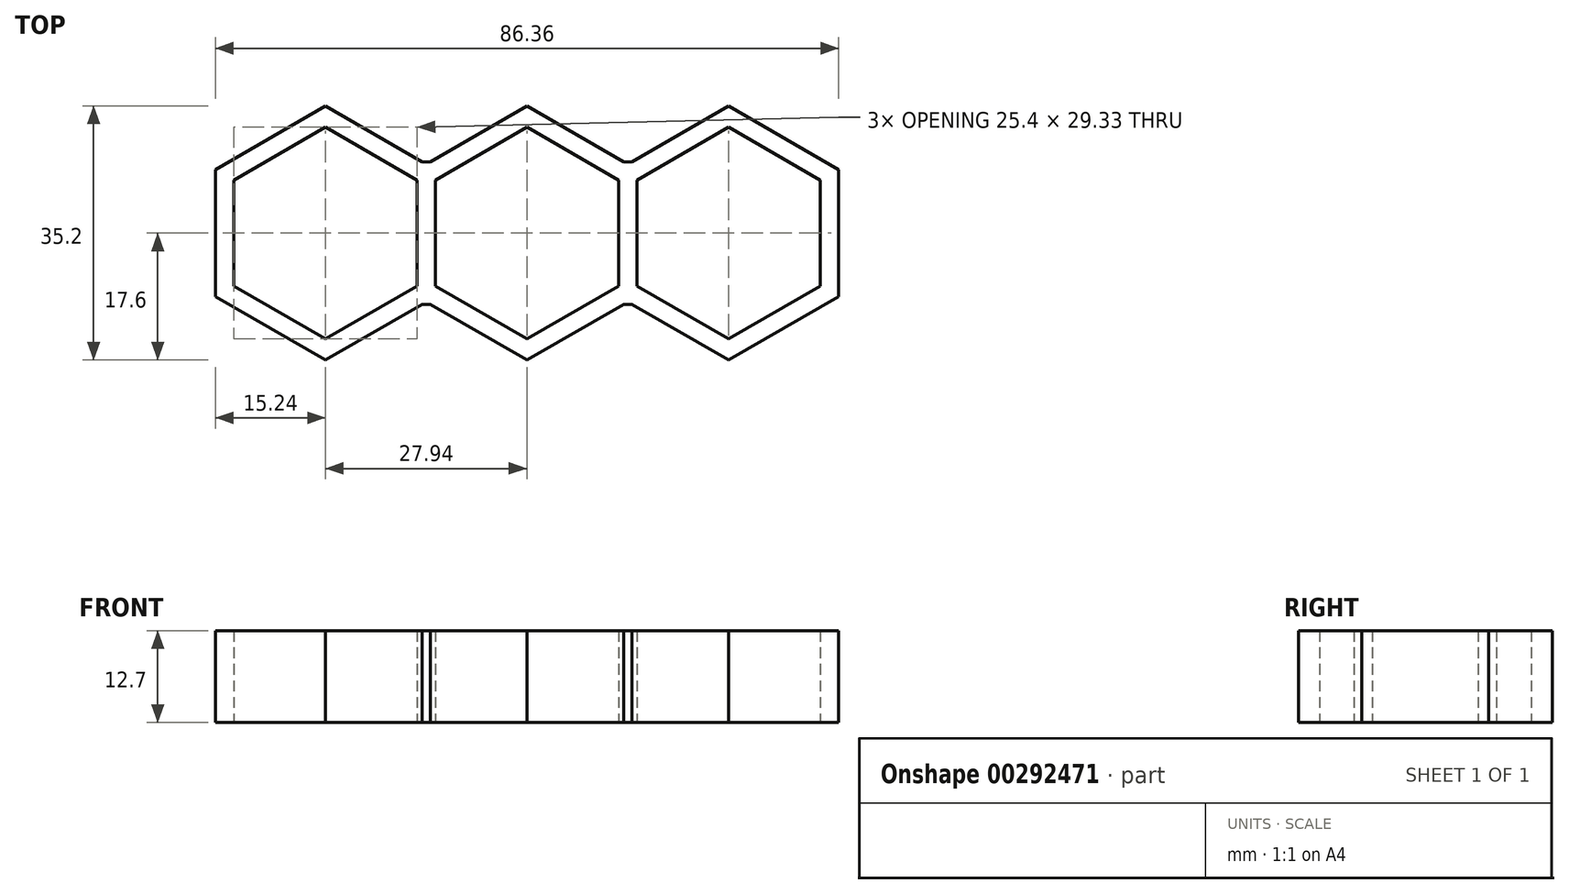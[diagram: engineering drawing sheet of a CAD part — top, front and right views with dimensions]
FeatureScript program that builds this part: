
annotation { "Feature Type Name" : "Feature", "Feature Type Description" : "" }
export const myFeature = defineFeature(function(context is Context, id is Id, definition is map)
    precondition{}
    {
        {
            var Q0;
            Q0=qCreatedBy(makeId("Top.planeOp"),FACE);
            var sketch = newSketch(context, id + "F0", { "sketchPlane" : qUnion([Q0])});
            skCircle(sketch, "E0.cCircle", {"center": v(0, 0) * mm, "radius": 12.7 * mm, "construction": true});
            skLineSegment(sketch, "E0.0", {"start": v(-12.7, -7.33) * mm, "end": v(-12.7, 7.33) * mm});
            skLineSegment(sketch, "E0.1", {"start": v(-12.7, 7.33) * mm, "end": v(0, 14.66) * mm});
            skLineSegment(sketch, "E0.2", {"start": v(0, 14.66) * mm, "end": v(12.7, 7.33) * mm});
            skLineSegment(sketch, "E0.3", {"start": v(12.7, 7.33) * mm, "end": v(12.7, -7.33) * mm});
            skLineSegment(sketch, "E0.4", {"start": v(12.7, -7.33) * mm, "end": v(0, -14.66) * mm});
            skLineSegment(sketch, "E0.5", {"start": v(0, -14.66) * mm, "end": v(-12.7, -7.33) * mm});
            skPoint(sketch, "E0.0.midPoint", {"position": v(-12.7, 0) * mm});
            skCircle(sketch, "E1.cCircle", {"center": v(-27.94, 0) * mm, "radius": 12.7 * mm, "construction": true});
            skLineSegment(sketch, "E1.0", {"start": v(-15.24, 7.33) * mm, "end": v(-15.24, -7.33) * mm});
            skLineSegment(sketch, "E1.1", {"start": v(-15.24, -7.33) * mm, "end": v(-27.94, -14.66) * mm});
            skLineSegment(sketch, "E1.2", {"start": v(-27.94, -14.66) * mm, "end": v(-40.64, -7.33) * mm});
            skLineSegment(sketch, "E1.3", {"start": v(-40.64, -7.33) * mm, "end": v(-40.64, 7.33) * mm});
            skLineSegment(sketch, "E1.4", {"start": v(-40.64, 7.33) * mm, "end": v(-27.94, 14.66) * mm});
            skLineSegment(sketch, "E1.5", {"start": v(-27.94, 14.66) * mm, "end": v(-15.24, 7.33) * mm});
            skPoint(sketch, "E1.0.midPoint", {"position": v(-15.24, 0) * mm});
            skCircle(sketch, "E2.cCircle", {"center": v(27.94, 0) * mm, "radius": 12.7 * mm, "construction": true});
            skLineSegment(sketch, "E2.0", {"start": v(15.24, -7.33) * mm, "end": v(15.24, 7.33) * mm});
            skLineSegment(sketch, "E2.1", {"start": v(15.24, 7.33) * mm, "end": v(27.94, 14.66) * mm});
            skLineSegment(sketch, "E2.2", {"start": v(27.94, 14.66) * mm, "end": v(40.64, 7.33) * mm});
            skLineSegment(sketch, "E2.3", {"start": v(40.64, 7.33) * mm, "end": v(40.64, -7.33) * mm});
            skLineSegment(sketch, "E2.4", {"start": v(40.64, -7.33) * mm, "end": v(27.94, -14.66) * mm});
            skLineSegment(sketch, "E2.5", {"start": v(27.94, -14.66) * mm, "end": v(15.24, -7.33) * mm});
            skPoint(sketch, "E2.0.midPoint", {"position": v(15.24, 0) * mm});
            skLineSegment(sketch, "E3.0", {"start": v(-43.18, -8.8) * mm, "end": v(-43.18, 8.8) * mm});
            skLineSegment(sketch, "E3.1", {"start": v(-27.94, -17.6) * mm, "end": v(-43.18, -8.8) * mm});
            skLineSegment(sketch, "E3.2", {"start": v(-14.56, -9.87) * mm, "end": v(-27.94, -17.6) * mm});
            skLineSegment(sketch, "E3.3", {"start": v(-14.56, -9.87) * mm, "end": v(-13.38, -9.87) * mm});
            skLineSegment(sketch, "E3.4", {"start": v(0, -17.6) * mm, "end": v(-13.38, -9.87) * mm});
            skLineSegment(sketch, "E3.5", {"start": v(-43.18, 8.8) * mm, "end": v(-27.94, 17.6) * mm});
            skLineSegment(sketch, "E3.6", {"start": v(13.38, -9.87) * mm, "end": v(0, -17.6) * mm});
            skLineSegment(sketch, "E3.7", {"start": v(13.38, -9.87) * mm, "end": v(14.56, -9.87) * mm});
            skLineSegment(sketch, "E3.8", {"start": v(0, 17.6) * mm, "end": v(13.38, 9.87) * mm});
            skLineSegment(sketch, "E3.9", {"start": v(-13.38, 9.87) * mm, "end": v(0, 17.6) * mm});
            skLineSegment(sketch, "E3.10", {"start": v(-14.56, 9.87) * mm, "end": v(-13.38, 9.87) * mm});
            skLineSegment(sketch, "E3.11", {"start": v(-27.94, 17.6) * mm, "end": v(-14.56, 9.87) * mm});
            skLineSegment(sketch, "E3.12", {"start": v(14.56, 9.87) * mm, "end": v(13.38, 9.87) * mm});
            skLineSegment(sketch, "E3.13", {"start": v(14.56, 9.87) * mm, "end": v(27.94, 17.6) * mm});
            skLineSegment(sketch, "E3.14", {"start": v(27.94, 17.6) * mm, "end": v(43.18, 8.8) * mm});
            skLineSegment(sketch, "E3.15", {"start": v(43.18, 8.8) * mm, "end": v(43.18, -8.8) * mm});
            skLineSegment(sketch, "E3.16", {"start": v(43.18, -8.8) * mm, "end": v(27.94, -17.6) * mm});
            skLineSegment(sketch, "E3.17", {"start": v(27.94, -17.6) * mm, "end": v(14.56, -9.87) * mm});
            skSolve(sketch);
        }
        {
            var Q0;
            Q0 = qSketchRegion(id + "F0", true);
            extrude(context, id + "F1", {"entities" : qUnion([Q0]), "depth" : 12.7 * mm});
        }
    });
